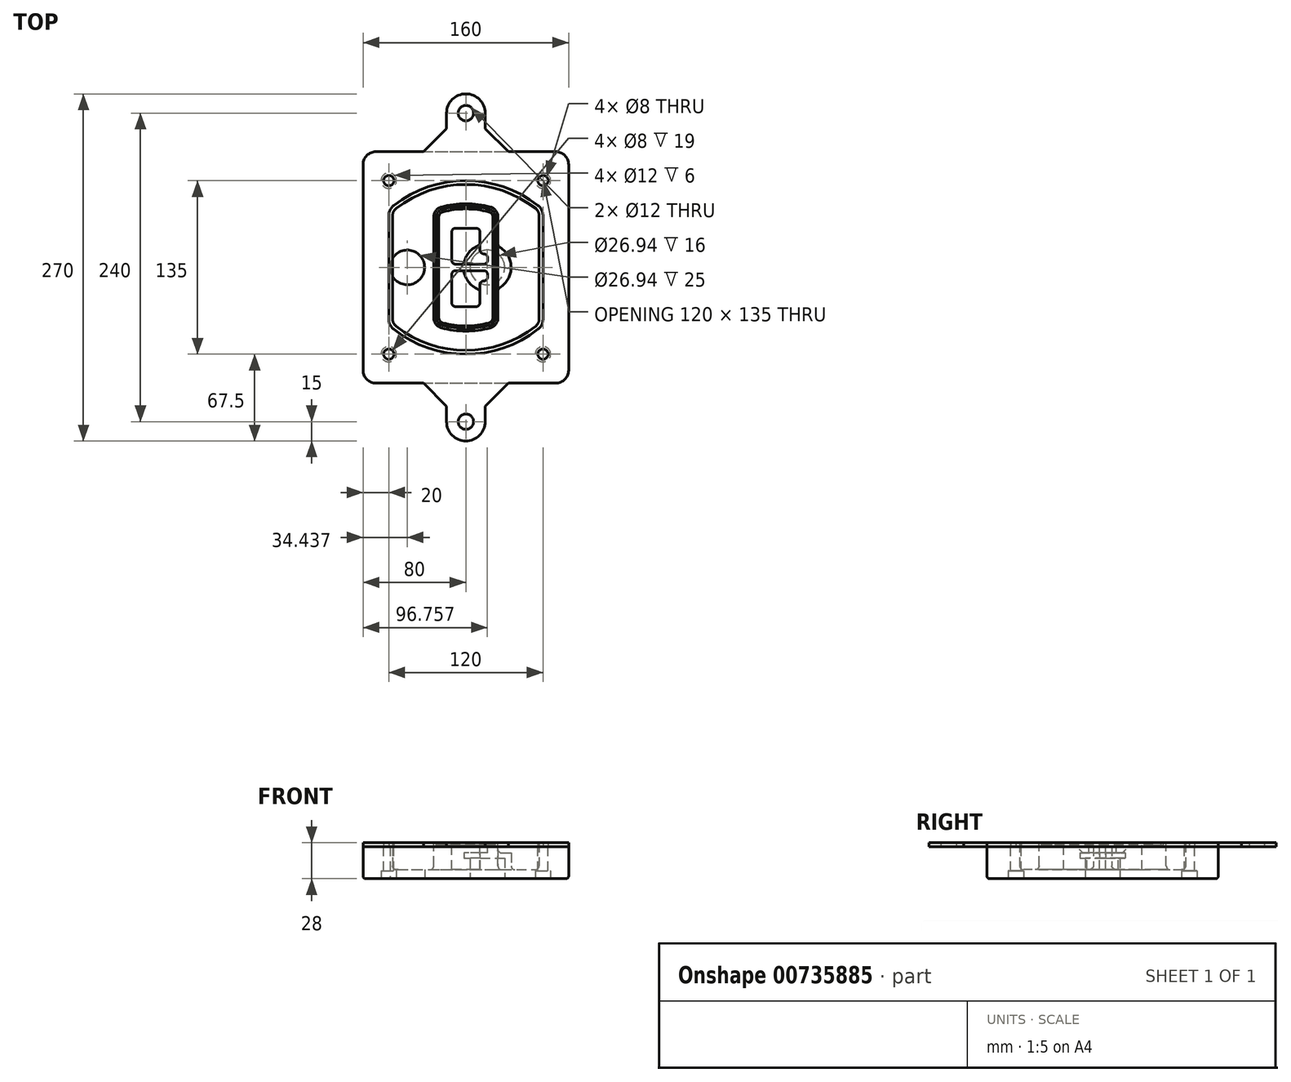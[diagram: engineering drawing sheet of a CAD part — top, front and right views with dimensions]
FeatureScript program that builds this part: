
annotation { "Feature Type Name" : "Feature", "Feature Type Description" : "" }
export const myFeature = defineFeature(function(context is Context, id is Id, definition is map)
    precondition{}
    {
        {
            var Q0;
            Q0=qCreatedBy(makeId("Top.planeOp"),FACE);
            var sketch = newSketch(context, id + "F0", { "sketchPlane" : qUnion([Q0])});
            skPoint(sketch, "E0.rect.middle", {"position": v(0, 0) * mm});
            skLineSegment(sketch, "E1.bottom", {"start": v(-70, -90) * mm, "end": v(70, -90) * mm});
            skLineSegment(sketch, "E1.top", {"start": v(-70, 90) * mm, "end": v(70, 90) * mm});
            skLineSegment(sketch, "E1.left", {"start": v(-80, -80) * mm, "end": v(-80, 80) * mm});
            skLineSegment(sketch, "E1.right", {"start": v(80, -80) * mm, "end": v(80, 80) * mm});
            skLineSegment(sketch, "E2", {"start": v(-80, 90) * mm, "end": v(80, -90) * mm, "construction": true});
            skLineSegment(sketch, "E3", {"start": v(80, 90) * mm, "end": v(-80, -90) * mm, "construction": true});
            skCircle(sketch, "E4", {"center": v(-60, 67.5) * mm, "radius": 4 * mm});
            skCircle(sketch, "E5", {"center": v(60, 67.5) * mm, "radius": 4 * mm});
            skCircle(sketch, "E6", {"center": v(60, -67.5) * mm, "radius": 4 * mm});
            skCircle(sketch, "E7", {"center": v(-60, -67.5) * mm, "radius": 4 * mm});
            skLineSegment(sketch, "E8", {"start": v(-60, 67.5) * mm, "end": v(60, 67.5) * mm, "construction": true});
            skLineSegment(sketch, "E9", {"start": v(60, 67.5) * mm, "end": v(60, -67.5) * mm, "construction": true});
            skLineSegment(sketch, "E10", {"start": v(60, -67.5) * mm, "end": v(-60, -67.5) * mm, "construction": true});
            skLineSegment(sketch, "E11", {"start": v(-60, -67.5) * mm, "end": v(-60, 67.5) * mm, "construction": true});
            skLineSegment(sketch, "E12", {"start": v(-60, 40.3) * mm, "end": v(-60, -40.3) * mm});
            skLineSegment(sketch, "E13", {"start": v(60, 40.3) * mm, "end": v(60, -40.3) * mm});
            skArc(sketch, "E14", {"start": v(56.15, 48.18) * mm, "mid": v(0, 67.5) * mm, "end": v(-56.15, 48.18) * mm});
            skArc(sketch, "E15", {"start": v(-56.15, -48.18) * mm, "mid": v(0, -67.5) * mm, "end": v(56.15, -48.18) * mm});
            skLineSegment(sketch, "E16", {"start": v(-60, 0) * mm, "end": v(60, 0) * mm, "construction": true});
            skPoint(sketch, "E17.visualSharp", {"position": v(-60, -45) * mm});
            skArc(sketch, "E17.filletArc", {"start": v(-60, -40.3) * mm, "mid": v(-58.99, -44.68) * mm, "end": v(-56.15, -48.18) * mm});
            skPoint(sketch, "E18.visualSharp", {"position": v(-60, 45) * mm});
            skArc(sketch, "E18.filletArc", {"start": v(-56.15, 48.18) * mm, "mid": v(-58.99, 44.68) * mm, "end": v(-60, 40.3) * mm});
            skPoint(sketch, "E19.visualSharp", {"position": v(60, 45) * mm});
            skArc(sketch, "E19.filletArc", {"start": v(60, 40.3) * mm, "mid": v(58.99, 44.68) * mm, "end": v(56.15, 48.18) * mm});
            skPoint(sketch, "E20.visualSharp", {"position": v(60, -45) * mm});
            skArc(sketch, "E20.filletArc", {"start": v(56.15, -48.18) * mm, "mid": v(58.99, -44.68) * mm, "end": v(60, -40.3) * mm});
            skPoint(sketch, "E21.visualSharp", {"position": v(-80, 90) * mm});
            skArc(sketch, "E21.filletArc", {"start": v(-70, 90) * mm, "mid": v(-77.07, 87.07) * mm, "end": v(-80, 80) * mm});
            skPoint(sketch, "E22.visualSharp", {"position": v(80, 90) * mm});
            skArc(sketch, "E22.filletArc", {"start": v(80, 80) * mm, "mid": v(77.07, 87.07) * mm, "end": v(70, 90) * mm});
            skPoint(sketch, "E23.visualSharp", {"position": v(80, -90) * mm});
            skArc(sketch, "E23.filletArc", {"start": v(70, -90) * mm, "mid": v(77.07, -87.07) * mm, "end": v(80, -80) * mm});
            skPoint(sketch, "E24.visualSharp", {"position": v(-80, -90) * mm});
            skArc(sketch, "E24.filletArc", {"start": v(-80, -80) * mm, "mid": v(-77.07, -87.07) * mm, "end": v(-70, -90) * mm});
            skArc(sketch, "E25.0", {"start": v(57, 40.3) * mm, "mid": v(56.3, 43.36) * mm, "end": v(54.3, 45.81) * mm});
            skLineSegment(sketch, "E25.1", {"start": v(57, 40.3) * mm, "end": v(57, -40.3) * mm});
            skArc(sketch, "E25.2", {"start": v(54.3, -45.81) * mm, "mid": v(56.3, -43.36) * mm, "end": v(57, -40.3) * mm});
            skArc(sketch, "E25.3", {"start": v(-54.3, -45.81) * mm, "mid": v(0, -64.5) * mm, "end": v(54.3, -45.81) * mm});
            skArc(sketch, "E25.4", {"start": v(-57, -40.3) * mm, "mid": v(-56.3, -43.36) * mm, "end": v(-54.3, -45.81) * mm});
            skArc(sketch, "E25.5", {"start": v(54.3, 45.81) * mm, "mid": v(0, 64.5) * mm, "end": v(-54.3, 45.81) * mm});
            skLineSegment(sketch, "E25.6", {"start": v(-57, 40.3) * mm, "end": v(-57, -40.3) * mm});
            skArc(sketch, "E25.7", {"start": v(-54.3, 45.81) * mm, "mid": v(-56.3, 43.36) * mm, "end": v(-57, 40.3) * mm});
            skArc(sketch, "E26.0", {"start": v(-58.62, 51.33) * mm, "mid": v(-62.58, 46.43) * mm, "end": v(-64, 40.3) * mm});
            skArc(sketch, "E26.1", {"start": v(58.62, 51.33) * mm, "mid": v(0, 71.5) * mm, "end": v(-58.62, 51.33) * mm});
            skArc(sketch, "E26.2", {"start": v(64, 40.3) * mm, "mid": v(62.58, 46.43) * mm, "end": v(58.62, 51.33) * mm});
            skLineSegment(sketch, "E26.3", {"start": v(64, 40.3) * mm, "end": v(64, -40.3) * mm});
            skArc(sketch, "E26.4", {"start": v(58.62, -51.33) * mm, "mid": v(62.58, -46.43) * mm, "end": v(64, -40.3) * mm});
            skLineSegment(sketch, "E26.5", {"start": v(-64, 40.3) * mm, "end": v(-64, -40.3) * mm});
            skArc(sketch, "E26.6", {"start": v(-58.62, -51.33) * mm, "mid": v(0, -71.5) * mm, "end": v(58.62, -51.33) * mm});
            skArc(sketch, "E26.7", {"start": v(-64, -40.3) * mm, "mid": v(-62.58, -46.43) * mm, "end": v(-58.62, -51.33) * mm});
            skSolve(sketch);
        }
        {
            var Q0;
            Q0=makeQuery(id+"F0.imprint","IMPRINT",FACE,{"disambiguationData":[TD([[makeQuery(id+"F0.imprint","IMPRINT",EDGE,{"derivedFrom":sQuery(id+"F0.wireOp",EDGE,"E1.bottom")}),1.0]])]});
            var Q1;
            Q1=makeQuery(id+"F0.imprint","IMPRINT",FACE,{"disambiguationData":[TD([[makeQuery(id+"F0.imprint","IMPRINT",EDGE,{"derivedFrom":sQuery(id+"F0.wireOp",EDGE,"E12")}),1.0]])]});
            var Q2;
            Q2=makeQuery(id+"F0.imprint","IMPRINT",FACE,{"disambiguationData":[TD([[makeQuery(id+"F0.imprint","IMPRINT",EDGE,{"derivedFrom":sQuery(id+"F0.wireOp",EDGE,"E25.0")}),1.0]])]});
            var Q3;
            Q3=makeQuery(id+"F0.imprint","IMPRINT",FACE,{"disambiguationData":[TD([[makeQuery(id+"F0.imprint","IMPRINT",EDGE,{"derivedFrom":sQuery(id+"F0.wireOp",EDGE,"E12")}),-1.0]])]});
            extrude(context, id + "F1", {"entities" : qUnion([Q0, Q1, Q2, Q3]), "oppositeDirection" : true, "depth" : 25 * mm});
        }
        {
            var Q0;
            Q0=makeQuery(id+"F0.imprint","IMPRINT",FACE,{"disambiguationData":[TD([[makeQuery(id+"F0.imprint","IMPRINT",EDGE,{"derivedFrom":sQuery(id+"F0.wireOp",EDGE,"E12")}),1.0]])]});
            extrude(context, id + "F2", {"entities" : qUnion([Q0]), "operationType" : NewBodyOperationType.ADD, "depth" : 3 * mm});
        }
        {
            var Q0;
            Q0=makeQuery(id+"F0.imprint","IMPRINT",FACE,{"disambiguationData":[TD([[makeQuery(id+"F0.imprint","IMPRINT",EDGE,{"derivedFrom":sQuery(id+"F0.wireOp",EDGE,"E25.0")}),1.0]])]});
            extrude(context, id + "F3", {"entities" : qUnion([Q0]), "operationType" : NewBodyOperationType.REMOVE, "oppositeDirection" : true, "depth" : 18 * mm});
        }
        {
            var Q0;
            Q0=makeQuery(id+"F2.opExtrude","CAP_FACE",FACE,{"disambiguationData":[OSD([sQuery(id+"F0.wireOp",EDGE,"E12"),sQuery(id+"F0.wireOp",EDGE,"E13"),sQuery(id+"F0.wireOp",EDGE,"E14"),sQuery(id+"F0.wireOp",EDGE,"E15"),sQuery(id+"F0.wireOp",EDGE,"E17.filletArc"),sQuery(id+"F0.wireOp",EDGE,"E18.filletArc"),sQuery(id+"F0.wireOp",EDGE,"E19.filletArc"),sQuery(id+"F0.wireOp",EDGE,"E20.filletArc"),sQuery(id+"F0.wireOp",EDGE,"E25.0"),sQuery(id+"F0.wireOp",EDGE,"E25.1"),sQuery(id+"F0.wireOp",EDGE,"E25.2"),sQuery(id+"F0.wireOp",EDGE,"E25.3"),sQuery(id+"F0.wireOp",EDGE,"E25.4"),sQuery(id+"F0.wireOp",EDGE,"E25.5"),sQuery(id+"F0.wireOp",EDGE,"E25.6"),sQuery(id+"F0.wireOp",EDGE,"E25.7")])],"isStart":false});
            var sketch = newSketch(context, id + "F4", { "sketchPlane" : qUnion([Q0])});
            skArc(sketch, "E27.0", {"start": v(-19.08, -46.97) * mm, "mid": v(0, -49.5) * mm, "end": v(19.08, -46.97) * mm});
            skArc(sketch, "E28.0", {"start": v(19.08, 46.97) * mm, "mid": v(0, 49.5) * mm, "end": v(-19.08, 46.97) * mm});
            skLineSegment(sketch, "E29", {"start": v(-25, 39.25) * mm, "end": v(-25, -39.25) * mm});
            skLineSegment(sketch, "E30", {"start": v(25, 39.25) * mm, "end": v(25, -39.25) * mm});
            skLineSegment(sketch, "E31", {"start": v(-25, 45.1) * mm, "end": v(25, 45.1) * mm, "construction": true});
            skLineSegment(sketch, "E32", {"start": v(-25, -45.1) * mm, "end": v(25, -45.1) * mm, "construction": true});
            skPoint(sketch, "E33.visualSharp", {"position": v(-25, 45.1) * mm});
            skArc(sketch, "E33.filletArc", {"start": v(-19.08, 46.97) * mm, "mid": v(-23.35, 44.11) * mm, "end": v(-25, 39.25) * mm});
            skPoint(sketch, "E34.visualSharp", {"position": v(25, 45.1) * mm});
            skArc(sketch, "E34.filletArc", {"start": v(25, 39.25) * mm, "mid": v(23.35, 44.11) * mm, "end": v(19.08, 46.97) * mm});
            skPoint(sketch, "E35.visualSharp", {"position": v(25, -45.1) * mm});
            skArc(sketch, "E35.filletArc", {"start": v(19.08, -46.97) * mm, "mid": v(23.35, -44.11) * mm, "end": v(25, -39.25) * mm});
            skPoint(sketch, "E36.visualSharp", {"position": v(-25, -45.1) * mm});
            skArc(sketch, "E36.filletArc", {"start": v(-25, -39.25) * mm, "mid": v(-23.35, -44.11) * mm, "end": v(-19.08, -46.97) * mm});
            skArc(sketch, "E37.0", {"start": v(54.3, 45.81) * mm, "mid": v(0, 64.5) * mm, "end": v(-54.3, 45.81) * mm});
            skArc(sketch, "E37.1", {"start": v(-54.3, 45.81) * mm, "mid": v(-56.3, 43.36) * mm, "end": v(-57, 40.3) * mm});
            skLineSegment(sketch, "E37.2", {"start": v(-57, 40.3) * mm, "end": v(-57, -40.3) * mm});
            skArc(sketch, "E37.3", {"start": v(-57, -40.3) * mm, "mid": v(-56.3, -43.36) * mm, "end": v(-54.3, -45.81) * mm});
            skArc(sketch, "E37.4", {"start": v(-54.3, -45.81) * mm, "mid": v(0, -64.5) * mm, "end": v(54.3, -45.81) * mm});
            skArc(sketch, "E37.5", {"start": v(54.3, -45.81) * mm, "mid": v(56.3, -43.36) * mm, "end": v(57, -40.3) * mm});
            skLineSegment(sketch, "E37.6", {"start": v(57, 40.3) * mm, "end": v(57, -40.3) * mm});
            skArc(sketch, "E37.7", {"start": v(57, 40.3) * mm, "mid": v(56.3, 43.36) * mm, "end": v(54.3, 45.81) * mm});
            skLineSegment(sketch, "E38.0", {"start": v(23, 39.25) * mm, "end": v(23, -39.25) * mm});
            skArc(sketch, "E38.1", {"start": v(18.56, -45.04) * mm, "mid": v(21.76, -42.9) * mm, "end": v(23, -39.25) * mm});
            skArc(sketch, "E38.2", {"start": v(-18.56, -45.04) * mm, "mid": v(0, -47.5) * mm, "end": v(18.56, -45.04) * mm});
            skArc(sketch, "E38.3", {"start": v(-23, -39.25) * mm, "mid": v(-21.76, -42.9) * mm, "end": v(-18.56, -45.04) * mm});
            skLineSegment(sketch, "E38.4", {"start": v(-23, 39.25) * mm, "end": v(-23, -39.25) * mm});
            skArc(sketch, "E38.5", {"start": v(23, 39.25) * mm, "mid": v(21.76, 42.9) * mm, "end": v(18.56, 45.04) * mm});
            skArc(sketch, "E38.6", {"start": v(-18.56, 45.04) * mm, "mid": v(-21.76, 42.9) * mm, "end": v(-23, 39.25) * mm});
            skArc(sketch, "E38.7", {"start": v(18.56, 45.04) * mm, "mid": v(0, 47.5) * mm, "end": v(-18.56, 45.04) * mm});
            skArc(sketch, "E39.0", {"start": v(21, 39.25) * mm, "mid": v(20.18, 41.68) * mm, "end": v(18.04, 43.1) * mm});
            skLineSegment(sketch, "E39.1", {"start": v(21, 39.25) * mm, "end": v(21, -39.25) * mm});
            skArc(sketch, "E39.2", {"start": v(18.04, -43.1) * mm, "mid": v(20.18, -41.68) * mm, "end": v(21, -39.25) * mm});
            skArc(sketch, "E39.3", {"start": v(-18.04, -43.1) * mm, "mid": v(0, -45.5) * mm, "end": v(18.04, -43.1) * mm});
            skArc(sketch, "E39.4", {"start": v(-21, -39.25) * mm, "mid": v(-20.18, -41.68) * mm, "end": v(-18.04, -43.1) * mm});
            skArc(sketch, "E39.5", {"start": v(18.04, 43.1) * mm, "mid": v(0, 45.5) * mm, "end": v(-18.04, 43.1) * mm});
            skLineSegment(sketch, "E39.6", {"start": v(-21, 39.25) * mm, "end": v(-21, -39.25) * mm});
            skArc(sketch, "E39.7", {"start": v(-18.04, 43.1) * mm, "mid": v(-20.18, 41.68) * mm, "end": v(-21, 39.25) * mm});
            skLineSegment(sketch, "E40", {"start": v(-25, 0) * mm, "end": v(25, 0) * mm, "construction": true});
            skLineSegment(sketch, "E41", {"start": v(-11, 5.5) * mm, "end": v(-11, 27.5) * mm});
            skLineSegment(sketch, "E42", {"start": v(-8, 30.5) * mm, "end": v(8, 30.5) * mm});
            skLineSegment(sketch, "E43", {"start": v(11, 27.5) * mm, "end": v(11, 13.5) * mm});
            skLineSegment(sketch, "E44", {"start": v(14, 10.5) * mm, "end": v(14, 10.5) * mm});
            skLineSegment(sketch, "E45", {"start": v(17, 7.5) * mm, "end": v(17, 5.5) * mm});
            skLineSegment(sketch, "E46", {"start": v(14, 2.5) * mm, "end": v(-8, 2.5) * mm});
            skPoint(sketch, "E47.visualSharp", {"position": v(-11, 30.5) * mm});
            skArc(sketch, "E47.filletArc", {"start": v(-8, 30.5) * mm, "mid": v(-10.12, 29.62) * mm, "end": v(-11, 27.5) * mm});
            skPoint(sketch, "E48.visualSharp", {"position": v(11, 30.5) * mm});
            skArc(sketch, "E48.filletArc", {"start": v(11, 27.5) * mm, "mid": v(10.12, 29.62) * mm, "end": v(8, 30.5) * mm});
            skPoint(sketch, "E49.visualSharp", {"position": v(11, 10.5) * mm});
            skArc(sketch, "E49.filletArc", {"start": v(11, 13.5) * mm, "mid": v(11.88, 11.38) * mm, "end": v(14, 10.5) * mm});
            skPoint(sketch, "E50.visualSharp", {"position": v(17, 10.5) * mm});
            skArc(sketch, "E50.filletArc", {"start": v(17, 7.5) * mm, "mid": v(16.12, 9.62) * mm, "end": v(14, 10.5) * mm});
            skPoint(sketch, "E51.visualSharp", {"position": v(17, 2.5) * mm});
            skArc(sketch, "E51.filletArc", {"start": v(14, 2.5) * mm, "mid": v(16.12, 3.38) * mm, "end": v(17, 5.5) * mm});
            skPoint(sketch, "E52.visualSharp", {"position": v(-11, 2.5) * mm});
            skArc(sketch, "E52.filletArc", {"start": v(-11, 5.5) * mm, "mid": v(-10.12, 3.38) * mm, "end": v(-8, 2.5) * mm});
            skLineSegment(sketch, "E53.0.MirrorCS", {"start": v(14, -2.5) * mm, "end": v(-8, -2.5) * mm});
            skArc(sketch, "E54.0.MirrorCS", {"start": v(-11, -5.5) * mm, "mid": v(-10.12, -3.38) * mm, "end": v(-8, -2.5) * mm});
            skLineSegment(sketch, "E55.0.MirrorCS", {"start": v(-11, -5.5) * mm, "end": v(-11, -27.5) * mm});
            skArc(sketch, "E56.0.MirrorCS", {"start": v(-8, -30.5) * mm, "mid": v(-10.12, -29.62) * mm, "end": v(-11, -27.5) * mm});
            skLineSegment(sketch, "E57.0.MirrorCS", {"start": v(-8, -30.5) * mm, "end": v(8, -30.5) * mm});
            skArc(sketch, "E58.0.MirrorCS", {"start": v(11, -27.5) * mm, "mid": v(10.12, -29.62) * mm, "end": v(8, -30.5) * mm});
            skLineSegment(sketch, "E59.0.MirrorCS", {"start": v(11, -27.5) * mm, "end": v(11, -13.5) * mm});
            skArc(sketch, "E60.0.MirrorCS", {"start": v(11, -13.5) * mm, "mid": v(11.88, -11.38) * mm, "end": v(14, -10.5) * mm});
            skArc(sketch, "E61.0.MirrorCS", {"start": v(17, -7.5) * mm, "mid": v(16.12, -9.62) * mm, "end": v(14, -10.5) * mm});
            skLineSegment(sketch, "E62.0.MirrorCS", {"start": v(17, -7.5) * mm, "end": v(17, -5.5) * mm});
            skArc(sketch, "E63.0.MirrorCS", {"start": v(14, -2.5) * mm, "mid": v(16.12, -3.38) * mm, "end": v(17, -5.5) * mm});
            skSolve(sketch);
        }
        {
            var Q0;
            Q0=makeQuery(id+"F4.imprint","IMPRINT",FACE,{"disambiguationData":[TD([[makeQuery(id+"F4.imprint","IMPRINT",EDGE,{"derivedFrom":sQuery(id+"F4.wireOp",EDGE,"E27.0")}),1.0]])]});
            var Q1;
            Q1=makeQuery(id+"F4.imprint","IMPRINT",FACE,{"disambiguationData":[TD([[makeQuery(id+"F4.imprint","IMPRINT",EDGE,{"derivedFrom":sQuery(id+"F4.wireOp",EDGE,"E38.0")}),-1.0]])]});
            var Q2;
            Q2=makeQuery(id+"F4.imprint","IMPRINT",FACE,{"disambiguationData":[TD([[makeQuery(id+"F4.imprint","IMPRINT",EDGE,{"derivedFrom":sQuery(id+"F4.wireOp",EDGE,"E39.0")}),1.0]])]});
            extrude(context, id + "F5", {"entities" : qUnion([Q0, Q1, Q2]), "operationType" : NewBodyOperationType.ADD, "endBound" : BoundingType.UP_TO_NEXT, "oppositeDirection" : true, "depth" : 25 * mm});
        }
        {
            var Q0;
            Q0=makeQuery(id+"F4.imprint","IMPRINT",FACE,{"disambiguationData":[TD([[makeQuery(id+"F4.imprint","IMPRINT",EDGE,{"derivedFrom":sQuery(id+"F4.wireOp",EDGE,"E38.0")}),-1.0]])]});
            extrude(context, id + "F6", {"entities" : qUnion([Q0]), "operationType" : NewBodyOperationType.REMOVE, "oppositeDirection" : true, "depth" : 2 * mm});
        }
        {
            var Q0;
            Q0=makeQuery(id+"F1.opExtrude","CAP_FACE",FACE,{"disambiguationData":[OSD([sQuery(id+"F0.wireOp",EDGE,"E1.bottom"),sQuery(id+"F0.wireOp",EDGE,"E1.top"),sQuery(id+"F0.wireOp",EDGE,"E1.left"),sQuery(id+"F0.wireOp",EDGE,"E1.right"),sQuery(id+"F0.wireOp",EDGE,"E4"),sQuery(id+"F0.wireOp",EDGE,"E5"),sQuery(id+"F0.wireOp",EDGE,"E6"),sQuery(id+"F0.wireOp",EDGE,"E7"),sQuery(id+"F0.wireOp",EDGE,"E21.filletArc"),sQuery(id+"F0.wireOp",EDGE,"E22.filletArc"),sQuery(id+"F0.wireOp",EDGE,"E23.filletArc"),sQuery(id+"F0.wireOp",EDGE,"E24.filletArc")])],"isStart":false});
            var sketch = newSketch(context, id + "F7", { "sketchPlane" : qUnion([Q0])});
            skCircle(sketch, "E64", {"center": v(16.76, 0) * mm, "radius": 13.47 * mm});
            skCircle(sketch, "E65", {"center": v(-45.56, 0) * mm, "radius": 13.47 * mm});
            skLineSegment(sketch, "E66", {"start": v(80, 0) * mm, "end": v(-80, 0) * mm});
            skCircle(sketch, "E67", {"center": v(16.76, 0) * mm, "radius": 18.47 * mm});
            skCircle(sketch, "E68", {"center": v(60, -67.5) * mm, "radius": 6 * mm});
            skCircle(sketch, "E69", {"center": v(-60, -67.5) * mm, "radius": 6 * mm});
            skCircle(sketch, "E70", {"center": v(-60, 67.5) * mm, "radius": 6 * mm});
            skCircle(sketch, "E71", {"center": v(60, 67.5) * mm, "radius": 6 * mm});
            skSolve(sketch);
        }
        {
            var Q0;
            {var subQ1=sQuery(id+"F7.wireOp",EDGE,"E66");var subQ4=sQuery(id+"F7.wireOp",EDGE,"E64");var subQ6=makeQuery(id+"F7.imprint","INTERSECT",VERTEX,{"disambiguationData":[OD(0.0)],"derivedFrom":[subQ4,subQ1]});Q0=makeQuery(id+"F7.imprint","IMPRINT",FACE,{"disambiguationData":[TD([[makeQuery(id+"F7.imprint","IMPRINT",EDGE,{"disambiguationData":[TD([[subQ6,-1.0]])],"derivedFrom":subQ4}),-1.0]])]});}
            var Q1;
            {var subQ0=sQuery(id+"F7.wireOp",EDGE,"E66");var subQ1=sQuery(id+"F7.wireOp",EDGE,"E64");var subQ3=makeQuery(id+"F7.imprint","INTERSECT",VERTEX,{"disambiguationData":[OD(0.0)],"derivedFrom":[subQ1,subQ0]});Q1=makeQuery(id+"F7.imprint","IMPRINT",FACE,{"disambiguationData":[TD([[makeQuery(id+"F7.imprint","IMPRINT",EDGE,{"disambiguationData":[TD([[subQ3,-1.0]])],"derivedFrom":subQ1}),1.0]])]});}
            var Q2;
            {var subQ0=sQuery(id+"F7.wireOp",EDGE,"E66");var subQ1=sQuery(id+"F7.wireOp",EDGE,"E64");var subQ3=makeQuery(id+"F7.imprint","INTERSECT",VERTEX,{"disambiguationData":[OD(0.0)],"derivedFrom":[subQ1,subQ0]});Q2=makeQuery(id+"F7.imprint","IMPRINT",FACE,{"disambiguationData":[TD([[makeQuery(id+"F7.imprint","IMPRINT",EDGE,{"disambiguationData":[TD([[subQ3,1.0]])],"derivedFrom":subQ1}),1.0]])]});}
            var Q3;
            {var subQ1=sQuery(id+"F7.wireOp",EDGE,"E66");var subQ4=sQuery(id+"F7.wireOp",EDGE,"E64");var subQ6=makeQuery(id+"F7.imprint","INTERSECT",VERTEX,{"disambiguationData":[OD(0.0)],"derivedFrom":[subQ4,subQ1]});Q3=makeQuery(id+"F7.imprint","IMPRINT",FACE,{"disambiguationData":[TD([[makeQuery(id+"F7.imprint","IMPRINT",EDGE,{"disambiguationData":[TD([[subQ6,1.0]])],"derivedFrom":subQ4}),-1.0]])]});}
            extrude(context, id + "F8", {"entities" : qUnion([Q0, Q1, Q2, Q3]), "operationType" : NewBodyOperationType.ADD, "oppositeDirection" : true, "depth" : 20 * mm});
        }
        {
            var Q0;
            {var subQ0=sQuery(id+"F7.wireOp",EDGE,"E66");var subQ1=sQuery(id+"F7.wireOp",EDGE,"E64");var subQ3=makeQuery(id+"F7.imprint","INTERSECT",VERTEX,{"disambiguationData":[OD(0.0)],"derivedFrom":[subQ1,subQ0]});Q0=makeQuery(id+"F7.imprint","IMPRINT",FACE,{"disambiguationData":[TD([[makeQuery(id+"F7.imprint","IMPRINT",EDGE,{"disambiguationData":[TD([[subQ3,-1.0]])],"derivedFrom":subQ1}),1.0]])]});}
            var Q1;
            {var subQ0=sQuery(id+"F7.wireOp",EDGE,"E66");var subQ1=sQuery(id+"F7.wireOp",EDGE,"E64");var subQ3=makeQuery(id+"F7.imprint","INTERSECT",VERTEX,{"disambiguationData":[OD(0.0)],"derivedFrom":[subQ1,subQ0]});Q1=makeQuery(id+"F7.imprint","IMPRINT",FACE,{"disambiguationData":[TD([[makeQuery(id+"F7.imprint","IMPRINT",EDGE,{"disambiguationData":[TD([[subQ3,1.0]])],"derivedFrom":subQ1}),1.0]])]});}
            extrude(context, id + "F9", {"entities" : qUnion([Q0, Q1]), "operationType" : NewBodyOperationType.REMOVE, "oppositeDirection" : true, "depth" : 16 * mm});
        }
        {
            var Q0;
            {var subQ0=sQuery(id+"F7.wireOp",EDGE,"E66");var subQ1=sQuery(id+"F7.wireOp",EDGE,"E65");var subQ3=makeQuery(id+"F7.imprint","INTERSECT",VERTEX,{"disambiguationData":[OD(0.0)],"derivedFrom":[subQ1,subQ0]});Q0=makeQuery(id+"F7.imprint","IMPRINT",FACE,{"disambiguationData":[TD([[makeQuery(id+"F7.imprint","IMPRINT",EDGE,{"disambiguationData":[TD([[subQ3,-1.0]])],"derivedFrom":subQ1}),1.0]])]});}
            var Q1;
            {var subQ0=sQuery(id+"F7.wireOp",EDGE,"E66");var subQ1=sQuery(id+"F7.wireOp",EDGE,"E65");var subQ3=makeQuery(id+"F7.imprint","INTERSECT",VERTEX,{"disambiguationData":[OD(0.0)],"derivedFrom":[subQ1,subQ0]});Q1=makeQuery(id+"F7.imprint","IMPRINT",FACE,{"disambiguationData":[TD([[makeQuery(id+"F7.imprint","IMPRINT",EDGE,{"disambiguationData":[TD([[subQ3,1.0]])],"derivedFrom":subQ1}),1.0]])]});}
            extrude(context, id + "F10", {"entities" : qUnion([Q0, Q1]), "operationType" : NewBodyOperationType.REMOVE, "oppositeDirection" : true, "depth" : 25 * mm});
        }
        {
            var Q0;
            Q0=makeQuery(id+"F7.imprint","IMPRINT",FACE,{"disambiguationData":[TD([[makeQuery(id+"F7.imprint","IMPRINT",EDGE,{"derivedFrom":sQuery(id+"F7.wireOp",EDGE,"E68")}),1.0]])]});
            var Q1;
            Q1=makeQuery(id+"F7.imprint","IMPRINT",FACE,{"disambiguationData":[TD([[makeQuery(id+"F7.imprint","IMPRINT",EDGE,{"derivedFrom":makeQuery(id+"F1.opExtrude","CAP_EDGE",EDGE,{"disambiguationData":[OSD([sQuery(id+"F0.wireOp",EDGE,"E5")])],"isStart":false})}),-1.0]])]});
            var Q2;
            Q2=makeQuery(id+"F7.imprint","IMPRINT",FACE,{"disambiguationData":[TD([[makeQuery(id+"F7.imprint","IMPRINT",EDGE,{"derivedFrom":sQuery(id+"F7.wireOp",EDGE,"E69")}),1.0]])]});
            var Q3;
            Q3=makeQuery(id+"F7.imprint","IMPRINT",FACE,{"disambiguationData":[TD([[makeQuery(id+"F7.imprint","IMPRINT",EDGE,{"derivedFrom":makeQuery(id+"F1.opExtrude","CAP_EDGE",EDGE,{"disambiguationData":[OSD([sQuery(id+"F0.wireOp",EDGE,"E4")])],"isStart":false})}),-1.0]])]});
            var Q4;
            Q4=makeQuery(id+"F7.imprint","IMPRINT",FACE,{"disambiguationData":[TD([[makeQuery(id+"F7.imprint","IMPRINT",EDGE,{"derivedFrom":sQuery(id+"F7.wireOp",EDGE,"E70")}),1.0]])]});
            var Q5;
            Q5=makeQuery(id+"F7.imprint","IMPRINT",FACE,{"disambiguationData":[TD([[makeQuery(id+"F7.imprint","IMPRINT",EDGE,{"derivedFrom":makeQuery(id+"F1.opExtrude","CAP_EDGE",EDGE,{"disambiguationData":[OSD([sQuery(id+"F0.wireOp",EDGE,"E7")])],"isStart":false})}),-1.0]])]});
            var Q6;
            Q6=makeQuery(id+"F7.imprint","IMPRINT",FACE,{"disambiguationData":[TD([[makeQuery(id+"F7.imprint","IMPRINT",EDGE,{"derivedFrom":sQuery(id+"F7.wireOp",EDGE,"E71")}),1.0]])]});
            var Q7;
            Q7=makeQuery(id+"F7.imprint","IMPRINT",FACE,{"disambiguationData":[TD([[makeQuery(id+"F7.imprint","IMPRINT",EDGE,{"derivedFrom":makeQuery(id+"F1.opExtrude","CAP_EDGE",EDGE,{"disambiguationData":[OSD([sQuery(id+"F0.wireOp",EDGE,"E6")])],"isStart":false})}),-1.0]])]});
            extrude(context, id + "F11", {"entities" : qUnion([Q0, Q1, Q2, Q3, Q4, Q5, Q6, Q7]), "operationType" : NewBodyOperationType.REMOVE, "oppositeDirection" : true, "depth" : 6 * mm});
        }
        {
            var Q0;
            Q0=makeQuery(id+"F9.boolean.opBoolean","COPY",FACE,{"derivedFrom":makeQuery(id+"F9.opExtrude","CAP_FACE",FACE,{"disambiguationData":[OSD([sQuery(id+"F7.wireOp",EDGE,"E64")])],"isStart":false})});
            var sketch = newSketch(context, id + "F12", { "sketchPlane" : qUnion([Q0])});
            skArc(sketch, "E72.0", {"start": v(11, 17.55) * mm, "mid": v(2.57, 11.82) * mm, "end": v(-1.54, 2.5) * mm});
            skArc(sketch, "E72.1", {"start": v(-1.54, -2.5) * mm, "mid": v(2.57, -11.82) * mm, "end": v(11, -17.55) * mm});
            skLineSegment(sketch, "E73", {"start": v(-1.54, -2.5) * mm, "end": v(14, -2.5) * mm});
            skLineSegment(sketch, "E74.0", {"start": v(14, 2.5) * mm, "end": v(-1.54, 2.5) * mm});
            skArc(sketch, "E74.1", {"start": v(14, 2.5) * mm, "mid": v(16.12, 3.38) * mm, "end": v(17, 5.5) * mm});
            skLineSegment(sketch, "E74.2", {"start": v(17, 7.5) * mm, "end": v(17, 5.5) * mm});
            skArc(sketch, "E74.3", {"start": v(17, 7.5) * mm, "mid": v(16.12, 9.62) * mm, "end": v(14, 10.5) * mm});
            skArc(sketch, "E74.4", {"start": v(11, 13.5) * mm, "mid": v(11.88, 11.38) * mm, "end": v(14, 10.5) * mm});
            skLineSegment(sketch, "E74.5", {"start": v(11, 17.55) * mm, "end": v(11, 13.5) * mm});
            skLineSegment(sketch, "E74.7", {"start": v(14, -2.5) * mm, "end": v(-1.54, -2.5) * mm});
            skArc(sketch, "E74.8", {"start": v(14, -2.5) * mm, "mid": v(16.12, -3.38) * mm, "end": v(17, -5.5) * mm});
            skLineSegment(sketch, "E74.9", {"start": v(17, -7.5) * mm, "end": v(17, -5.5) * mm});
            skArc(sketch, "E74.10", {"start": v(17, -7.5) * mm, "mid": v(16.12, -9.62) * mm, "end": v(14, -10.5) * mm});
            skArc(sketch, "E74.11", {"start": v(11, -13.5) * mm, "mid": v(11.88, -11.38) * mm, "end": v(14, -10.5) * mm});
            skLineSegment(sketch, "E74.12", {"start": v(11, -17.55) * mm, "end": v(11, -13.5) * mm});
            skPoint(sketch, "E75.orphan", {"position": v(11, -27.5) * mm});
            skPoint(sketch, "E76.orphan", {"position": v(-8, -2.5) * mm});
            skPoint(sketch, "E77.orphan", {"position": v(-8, 2.5) * mm});
            skPoint(sketch, "E78.orphan", {"position": v(11, 27.5) * mm});
            skSolve(sketch);
        }
        {
            var Q0;
            {var subQ7=sQuery(id+"F12.wireOp",EDGE,"E72.0");var subQ14=sQuery(id+"F12.wireOp",EDGE,"E72.1");var subQ16=sQuery(id+"F12.wireOp",EDGE,"E74.1");var subQ18=sQuery(id+"F12.wireOp",EDGE,"E74.8");Q0=qUnion([makeQuery(id+"F12.imprint","IMPRINT",FACE,{"disambiguationData":[TD([[makeQuery(id+"F12.imprint","IMPRINT",EDGE,{"derivedFrom":subQ7}),1.0]])]}),makeQuery(id+"F12.imprint","IMPRINT",FACE,{"disambiguationData":[TD([[makeQuery(id+"F12.imprint","IMPRINT",EDGE,{"derivedFrom":subQ14}),1.0]])]}),makeQuery(id+"F12.imprint","IMPRINT",FACE,{"disambiguationData":[TD([[makeQuery(id+"F12.imprint","IMPRINT",EDGE,{"derivedFrom":subQ16}),1.0]])]}),makeQuery(id+"F12.imprint","IMPRINT",FACE,{"disambiguationData":[TD([[makeQuery(id+"F12.imprint","IMPRINT",EDGE,{"derivedFrom":subQ18}),-1.0]])]})]);}
            var Q1;
            Q1=makeQuery(id+"F5.boolean.opBoolean","SPLIT",FACE,{"disambiguationData":[TD([makeQuery(id+"F5.opExtrude","SWEPT_FACE",FACE,{"disambiguationData":[OSD([sQuery(id+"F4.wireOp",EDGE,"E41")])]})])],"derivedFrom":makeQuery(id+"F3.boolean.opBoolean","COPY",FACE,{"derivedFrom":makeQuery(id+"F3.opExtrude","CAP_FACE",FACE,{"disambiguationData":[OSD([sQuery(id+"F0.wireOp",EDGE,"E25.0"),sQuery(id+"F0.wireOp",EDGE,"E25.1"),sQuery(id+"F0.wireOp",EDGE,"E25.2"),sQuery(id+"F0.wireOp",EDGE,"E25.3"),sQuery(id+"F0.wireOp",EDGE,"E25.4"),sQuery(id+"F0.wireOp",EDGE,"E25.5"),sQuery(id+"F0.wireOp",EDGE,"E25.6"),sQuery(id+"F0.wireOp",EDGE,"E25.7")])],"isStart":false})})});
            extrude(context, id + "F13", {"entities" : qUnion([Q0]), "operationType" : NewBodyOperationType.REMOVE, "endBound" : BoundingType.UP_TO_SURFACE, "endBoundEntityFace" : qUnion([Q1]), "depth" : 25 * mm});
        }
        {
            var Q0;
            Q0=makeQuery(id+"F3.boolean.opBoolean","COPY",EDGE,{"derivedFrom":makeQuery(id+"F3.opExtrude","CAP_EDGE",EDGE,{"disambiguationData":[OSD([sQuery(id+"F0.wireOp",EDGE,"E25.6")])],"isStart":false})});
            var Q1;
            Q1=makeQuery(id+"F8.boolean.opBoolean","INTERSECT",EDGE,{"derivedFrom":[makeQuery(id+"F5.opExtrude","SWEPT_FACE",FACE,{"disambiguationData":[OSD([sQuery(id+"F4.wireOp",EDGE,"E30")])]}),makeQuery(id+"F8.opExtrude","CAP_FACE",FACE,{"disambiguationData":[OSD([sQuery(id+"F7.wireOp",EDGE,"E67")])],"isStart":false})]});
            var Q2;
            Q2=makeQuery(id+"F8.boolean.opBoolean","INTERSECT",EDGE,{"disambiguationData":[OD(1.0)],"derivedFrom":[makeQuery(id+"F5.opExtrude","SWEPT_FACE",FACE,{"disambiguationData":[OSD([sQuery(id+"F4.wireOp",EDGE,"E30")])]}),makeQuery(id+"F8.opExtrude","SWEPT_FACE",FACE,{"disambiguationData":[OSD([sQuery(id+"F7.wireOp",EDGE,"E67")])]})]});
            var Q3;
            {var subQ0=sQuery(id+"F4.wireOp",EDGE,"E30");Q3=makeQuery(id+"F8.boolean.opBoolean","SPLIT",EDGE,{"disambiguationData":[TD([makeQuery(id+"F5.opExtrude","SWEPT_FACE",FACE,{"disambiguationData":[OSD([sQuery(id+"F4.wireOp",EDGE,"E35.filletArc")])]})])],"derivedFrom":makeQuery(id+"F5.opExtrude","CAP_EDGE",EDGE,{"disambiguationData":[OSD([subQ0])],"isStart":false})});}
            var Q4;
            {var subQ0=sQuery(id+"F0.wireOp",EDGE,"E25.7");var subQ1=sQuery(id+"F0.wireOp",EDGE,"E25.1");var subQ2=sQuery(id+"F0.wireOp",EDGE,"E25.6");var subQ3=sQuery(id+"F0.wireOp",EDGE,"E25.5");var subQ4=sQuery(id+"F0.wireOp",EDGE,"E25.4");var subQ5=sQuery(id+"F0.wireOp",EDGE,"E25.0");var subQ6=sQuery(id+"F0.wireOp",EDGE,"E25.2");var subQ7=sQuery(id+"F0.wireOp",EDGE,"E25.3");Q4=makeQuery(id+"F8.boolean.opBoolean","INTERSECT",EDGE,{"derivedFrom":[makeQuery(id+"F5.boolean.opBoolean","SPLIT",FACE,{"disambiguationData":[TD([makeQuery(id+"F2.opExtrude","SWEPT_FACE",FACE,{"disambiguationData":[OSD([subQ5])]})])],"derivedFrom":makeQuery(id+"F3.boolean.opBoolean","COPY",FACE,{"derivedFrom":makeQuery(id+"F3.opExtrude","CAP_FACE",FACE,{"disambiguationData":[OSD([subQ5,subQ1,subQ6,subQ7,subQ4,subQ3,subQ2,subQ0])],"isStart":false})})}),makeQuery(id+"F8.opExtrude","SWEPT_FACE",FACE,{"disambiguationData":[OSD([sQuery(id+"F7.wireOp",EDGE,"E67")])]})]});}
            var Q5;
            Q5=makeQuery(id+"F8.boolean.opBoolean","INTERSECT",EDGE,{"disambiguationData":[OD(0.0)],"derivedFrom":[makeQuery(id+"F5.opExtrude","SWEPT_FACE",FACE,{"disambiguationData":[OSD([sQuery(id+"F4.wireOp",EDGE,"E30")])]}),makeQuery(id+"F8.opExtrude","SWEPT_FACE",FACE,{"disambiguationData":[OSD([sQuery(id+"F7.wireOp",EDGE,"E67")])]})]});
            fillet(context, id + "F14", {"entities" : qUnion([Q0, Q1, Q2, Q3, Q4, Q5]), "radius" : 3 * mm, "tangentPropagation" : true, "allowEdgeOverflow" : false});
        }
        {
            var Q0;
            Q0=makeQuery(id+"F1.opExtrude","CAP_EDGE",EDGE,{"disambiguationData":[OSD([sQuery(id+"F0.wireOp",EDGE,"E1.bottom")])],"isStart":false});
            fillet(context, id + "F15", {"entities" : qUnion([Q0]), "radius" : 2 * mm, "tangentPropagation" : true, "allowEdgeOverflow" : false});
        }
        {
            var Q0;
            {var subQ0=sQuery(id+"F0.wireOp",EDGE,"E21.filletArc");var subQ1=sQuery(id+"F0.wireOp",EDGE,"E7");var subQ2=sQuery(id+"F0.wireOp",EDGE,"E6");var subQ3=sQuery(id+"F0.wireOp",EDGE,"E5");var subQ4=sQuery(id+"F0.wireOp",EDGE,"E4");var subQ5=sQuery(id+"F0.wireOp",EDGE,"E22.filletArc");var subQ6=sQuery(id+"F0.wireOp",EDGE,"E1.bottom");var subQ7=sQuery(id+"F0.wireOp",EDGE,"E1.right");var subQ8=sQuery(id+"F0.wireOp",EDGE,"E1.top");var subQ9=sQuery(id+"F0.wireOp",EDGE,"E1.left");var subQ10=sQuery(id+"F0.wireOp",EDGE,"E23.filletArc");var subQ11=sQuery(id+"F0.wireOp",EDGE,"E24.filletArc");Q0=makeQuery(id+"F2.boolean.opBoolean","SPLIT",FACE,{"disambiguationData":[TD([makeQuery(id+"F1.opExtrude","SWEPT_FACE",FACE,{"disambiguationData":[OSD([subQ6])]})])],"derivedFrom":makeQuery(id+"F1.opExtrude","CAP_FACE",FACE,{"disambiguationData":[OSD([subQ6,subQ8,subQ9,subQ7,subQ4,subQ3,subQ2,subQ1,subQ0,subQ5,subQ10,subQ11])],"isStart":true})});}
            var sketch = newSketch(context, id + "F16", { "sketchPlane" : qUnion([Q0])});
            skLineSegment(sketch, "E79", {"start": v(0, 90) * mm, "end": v(0, 120) * mm, "construction": true});
            skLineSegment(sketch, "E80", {"start": v(-33, 90) * mm, "end": v(-15, 108) * mm});
            skLineSegment(sketch, "E81", {"start": v(33, 90) * mm, "end": v(15, 108) * mm});
            skLineSegment(sketch, "E82", {"start": v(-15, 108) * mm, "end": v(-15, 120) * mm});
            skLineSegment(sketch, "E83", {"start": v(15, 108) * mm, "end": v(15, 120) * mm});
            skCircle(sketch, "E84", {"center": v(0, 120) * mm, "radius": 6 * mm});
            skArc(sketch, "E85", {"start": v(15, 120) * mm, "mid": v(0, 135) * mm, "end": v(-15, 120) * mm});
            skLineSegment(sketch, "E86", {"start": v(-80, 0) * mm, "end": v(80, 0) * mm, "construction": true});
            skLineSegment(sketch, "E87.MirrorCS", {"start": v(-15, -108) * mm, "end": v(-15, -120) * mm});
            skLineSegment(sketch, "E88.MirrorCS", {"start": v(15, -108) * mm, "end": v(15, -120) * mm});
            skLineSegment(sketch, "E89.MirrorCS", {"start": v(0, -90) * mm, "end": v(0, -120) * mm, "construction": true});
            skLineSegment(sketch, "E90.MirrorCS", {"start": v(33, -90) * mm, "end": v(15, -108) * mm});
            skLineSegment(sketch, "E91.MirrorCS", {"start": v(-33, -90) * mm, "end": v(-15, -108) * mm});
            skCircle(sketch, "E92.MirrorC", {"center": v(0, -120) * mm, "radius": 6 * mm});
            skArc(sketch, "E93.MirrorCS", {"start": v(15, -120) * mm, "mid": v(0, -135) * mm, "end": v(-15, -120) * mm});
            skSolve(sketch);
        }
        {
            var Q0;
            {var subQ0=sQuery(id+"F16.wireOp",EDGE,"E80");Q0=makeQuery(id+"F16.imprint","IMPRINT",FACE,{"disambiguationData":[TD([[makeQuery(id+"F16.imprint","IMPRINT",EDGE,{"derivedFrom":subQ0}),-1.0]])]});}
            var Q1;
            Q1=makeQuery(id+"F16.imprint","IMPRINT",FACE,{"disambiguationData":[TD([[makeQuery(id+"F16.imprint","IMPRINT",EDGE,{"derivedFrom":sQuery(id+"F16.wireOp",EDGE,"E87.MirrorCS")}),1.0]])]});
            var Q2;
            Q2=makeQuery(id+"F16.imprint","IMPRINT",FACE,{"disambiguationData":[TD([[makeQuery(id+"F16.imprint","IMPRINT",EDGE,{"derivedFrom":makeQuery(id+"F1.opExtrude","CAP_EDGE",EDGE,{"disambiguationData":[OSD([sQuery(id+"F0.wireOp",EDGE,"E1.left")])],"isStart":true})}),-1.0]])]});
            var Q3;
            Q3=makeQuery(id+"F2.opExtrude","CAP_FACE",FACE,{"disambiguationData":[OSD([sQuery(id+"F0.wireOp",EDGE,"E12"),sQuery(id+"F0.wireOp",EDGE,"E13"),sQuery(id+"F0.wireOp",EDGE,"E14"),sQuery(id+"F0.wireOp",EDGE,"E15"),sQuery(id+"F0.wireOp",EDGE,"E17.filletArc"),sQuery(id+"F0.wireOp",EDGE,"E18.filletArc"),sQuery(id+"F0.wireOp",EDGE,"E19.filletArc"),sQuery(id+"F0.wireOp",EDGE,"E20.filletArc"),sQuery(id+"F0.wireOp",EDGE,"E25.0"),sQuery(id+"F0.wireOp",EDGE,"E25.1"),sQuery(id+"F0.wireOp",EDGE,"E25.2"),sQuery(id+"F0.wireOp",EDGE,"E25.3"),sQuery(id+"F0.wireOp",EDGE,"E25.4"),sQuery(id+"F0.wireOp",EDGE,"E25.5"),sQuery(id+"F0.wireOp",EDGE,"E25.6"),sQuery(id+"F0.wireOp",EDGE,"E25.7")])],"isStart":false});
            extrude(context, id + "F17", {"entities" : qUnion([Q0, Q1, Q2]), "endBound" : BoundingType.UP_TO_SURFACE, "depth" : 25 * mm, "endBoundEntityFace" : qUnion([Q3]), "offsetDistance" : 25 * mm});
        }
    });
